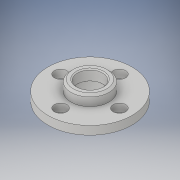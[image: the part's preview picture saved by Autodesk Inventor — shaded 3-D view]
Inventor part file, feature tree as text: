
AUTODESK INVENTOR PART (.ipt)
format: ipt  version: 2019 (Build 230136000, 136)  size: 146,432 bytes
history: native  units: mm
features: extrude x2, chamfer x2, sketch x2
ambient origin geometry x8: Origin, YZ Plane, XZ Plane, XY Plane, X Axis, Y Axis, Z Axis, Center Point
bodies: Solid1 (feature_tree)
feature tree (6):
  extrude  "Extrusion1"  Depth=6.05mm
  extrude  "Extrusion2"  Depth=3.0mm
  chamfer  "Chamfer1"  Distance=40.0mm Angle=360.0deg
  chamfer  "Chamfer2"  Distance=2.0mm
  sketch  "Sketch1"  dims[d0=20.0mm d1=6.05mm]
  sketch  "Sketch2"  dims[d2=14.0mm d3=3.0mm d4=40.0mm d6=360.0deg d8=2.0mm d9=0.0mm d10=6.0mm d11=9.0mm d12=2.5mm d13=0.0mm d14=0.5mm d15=2.0mm d16=45.0deg d17=0.25mm d18=2.0mm d19=45.0deg]
